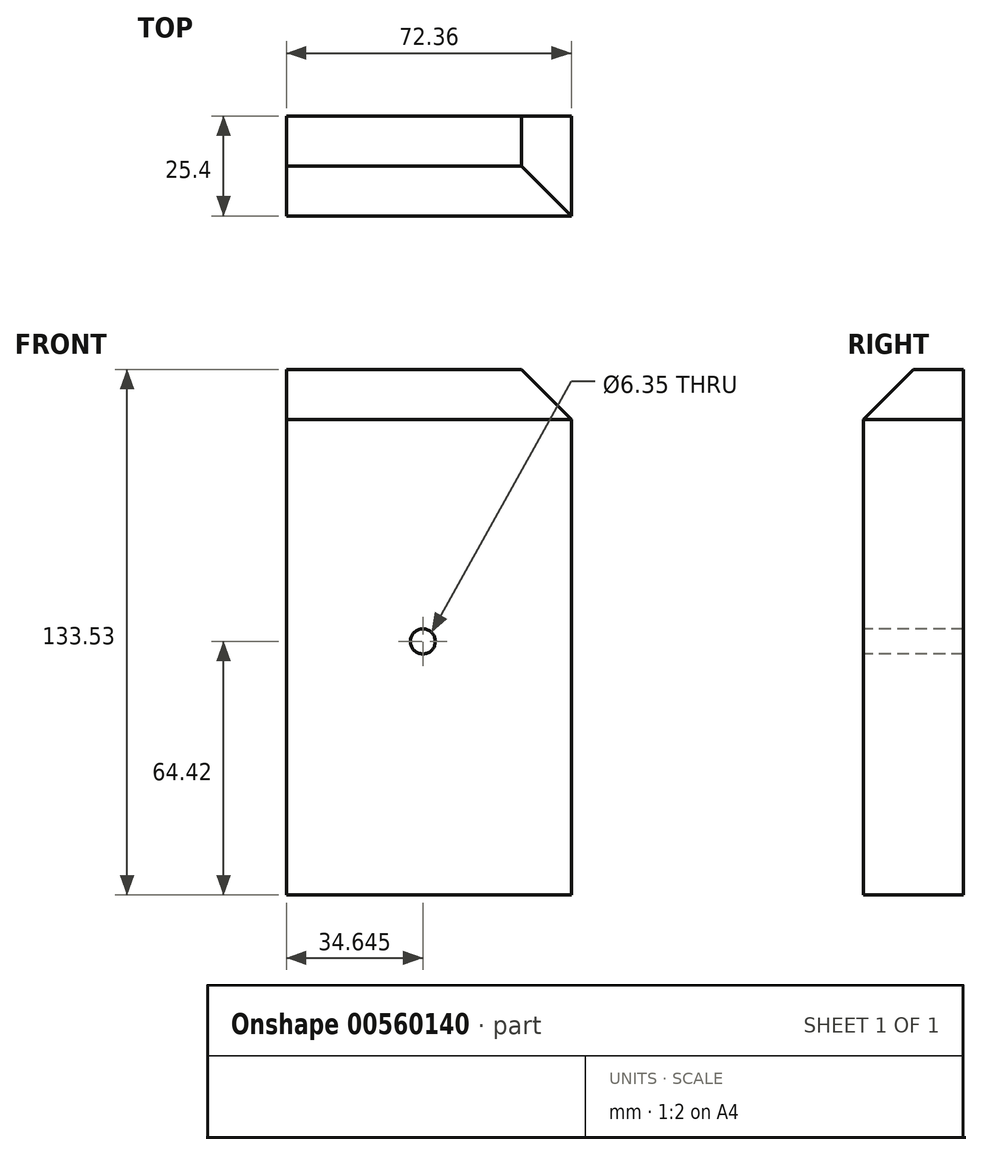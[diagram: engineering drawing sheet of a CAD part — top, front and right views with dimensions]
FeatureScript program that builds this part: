
annotation { "Feature Type Name" : "Feature", "Feature Type Description" : "" }
export const myFeature = defineFeature(function(context is Context, id is Id, definition is map)
    precondition{}
    {
        {
            var Q0;
            Q0=qCreatedBy(makeId("Front.planeOp"),FACE);
            var sketch = newSketch(context, id + "F0", { "sketchPlane" : qUnion([Q0])});
            skLineSegment(sketch, "E0", {"start": v(0, 16.42) * mm, "end": v(0, 69.11) * mm});
            skLineSegment(sketch, "E1", {"start": v(0, 69.11) * mm, "end": v(72.36, 69.11) * mm});
            skLineSegment(sketch, "E2", {"start": v(72.36, 69.11) * mm, "end": v(72.36, -64.42) * mm});
            skLineSegment(sketch, "E3", {"start": v(72.36, -64.42) * mm, "end": v(0, -64.42) * mm});
            skLineSegment(sketch, "E4", {"start": v(0, -64.42) * mm, "end": v(0, 16.42) * mm});
            skSolve(sketch);
        }
        {
            var Q0;
            Q0=makeQuery(id+"F0.imprint","IMPRINT",FACE,{"disambiguationData":[TD([[makeQuery(id+"F0.imprint","IMPRINT",EDGE,{"derivedFrom":sQuery(id+"F0.wireOp",EDGE,"E0")}),-1.0]])]});
            extrude(context, id + "F1", {"entities" : qUnion([Q0]), "depth" : 25.4 * mm, "offsetDistance" : 25.4 * mm});
        }
        {
            var Q0;
            Q0=makeQuery(id+"F1.opExtrude","CAP_FACE",FACE,{"disambiguationData":[OSD([sQuery(id+"F0.wireOp",EDGE,"E0"),sQuery(id+"F0.wireOp",EDGE,"E1"),sQuery(id+"F0.wireOp",EDGE,"E2"),sQuery(id+"F0.wireOp",EDGE,"E3"),sQuery(id+"F0.wireOp",EDGE,"E4")])],"isStart":false});
            var sketch = newSketch(context, id + "F2", { "sketchPlane" : qUnion([Q0])});
            skPoint(sketch, "E5", {"position": v(34.65, 0) * mm});
            skSolve(sketch);
        }
        {
            var Q0;
            Q0=sQuery(id+"F2.wireOp",VERTEX,"E5");
            var Q1;
            Q1=makeQuery(id+"F1.opExtrude","SWEPT_BODY",BODY,{"disambiguationData":[OSD([sQuery(id+"F0.wireOp",EDGE,"E0"),sQuery(id+"F0.wireOp",EDGE,"E1"),sQuery(id+"F0.wireOp",EDGE,"E2"),sQuery(id+"F0.wireOp",EDGE,"E3"),sQuery(id+"F0.wireOp",EDGE,"E4")])]});
            hole(context, id + "F3", {"style" : HoleStyle.SIMPLE, "endStyle" : HoleEndStyle.THROUGH, "holeDiameter" : 6.35 * mm, "isTappedThrough" : true, "tappedDepth" : 12.7 * mm, "tapClearance" : 3, "locations" : qUnion([Q0]), "scope" : qUnion([Q1])});
        }
        {
            var Q0;
            Q0=makeQuery(id+"F1.opExtrude","CAP_EDGE",EDGE,{"disambiguationData":[OSD([sQuery(id+"F0.wireOp",EDGE,"E1")])],"isStart":false});
            var Q1;
            Q1=makeQuery(id+"F1.opExtrude","SWEPT_EDGE",EDGE,{"disambiguationData":[OSD([sQuery(id+"F0.wireOp",EDGE,"E1"),sQuery(id+"F0.wireOp",EDGE,"E2")])]});
            chamfer(context, id + "F4", {"entities" : qUnion([Q0, Q1]), "width" : 12.7 * mm, "tangentPropagation" : true});
        }
    });
